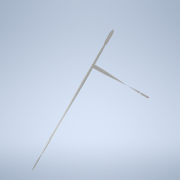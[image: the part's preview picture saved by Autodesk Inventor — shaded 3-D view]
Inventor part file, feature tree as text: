
AUTODESK INVENTOR PART (.ipt)
format: ipt  version: 2021 (Build 250183000, 183)  size: 4,764,160 bytes
history: native  units: in
note: dims shown in document units (in); Inventor stores cm internally (conversion verified against a paired STEP export)
features: imported_body x51, sketch x1
ambient origin geometry x8: Origin, YZ Plane, XZ Plane, XY Plane, X Axis, Y Axis, Z Axis, Center Point
bodies: Solid52 (feature_tree), Solid53 (feature_tree), Solid54 (feature_tree), Solid55 (feature_tree), Solid56 (feature_tree), Solid57 (feature_tree), Solid58 (feature_tree), Solid59 (feature_tree), Solid60 (feature_tree), Solid61 (feature_tree), Solid62 (feature_tree), Solid63 (feature_tree), Solid64 (feature_tree), Solid65 (feature_tree), Solid66 (feature_tree), Solid67 (feature_tree), Solid68 (feature_tree), Solid69 (feature_tree), Solid70 (feature_tree), Solid71 (feature_tree), Solid72 (feature_tree), Solid73 (feature_tree), Solid74 (feature_tree), Solid75 (feature_tree), Solid76 (feature_tree), Solid77 (feature_tree), Solid78 (feature_tree), Solid79 (feature_tree), Solid80 (feature_tree), Solid81 (feature_tree), Solid82 (feature_tree), Solid83 (feature_tree), Solid84 (feature_tree), Solid85 (feature_tree), Solid86 (feature_tree), Solid87 (feature_tree), Solid88 (feature_tree), Solid89 (feature_tree), Solid90 (feature_tree), Solid91 (feature_tree), Solid92 (feature_tree), Solid93 (feature_tree), Solid94 (feature_tree), Solid95 (feature_tree), Solid96 (feature_tree), Solid97 (feature_tree), Solid98 (feature_tree), Solid99 (feature_tree), Solid100 (feature_tree), Solid101 (feature_tree), Solid102 (feature_tree)
feature tree (52):
  imported_body  "Base52"
  sketch  "Sketch2"
  imported_body  "Base53"
  imported_body  "Base54"
  imported_body  "Base55"
  imported_body  "Base56"
  imported_body  "Base57"
  imported_body  "Base58"
  imported_body  "Base59"
  imported_body  "Base60"
  imported_body  "Base61"
  imported_body  "Base62"
  imported_body  "Base63"
  imported_body  "Base64"
  imported_body  "Base65"
  imported_body  "Base66"
  imported_body  "Base67"
  imported_body  "Base68"
  imported_body  "Base69"
  imported_body  "Base70"
  imported_body  "Base71"
  imported_body  "Base72"
  imported_body  "Base73"
  imported_body  "Base74"
  imported_body  "Base75"
  imported_body  "Base76"
  imported_body  "Base77"
  imported_body  "Base78"
  imported_body  "Base79"
  imported_body  "Base80"
  imported_body  "Base81"
  imported_body  "Base82"
  imported_body  "Base83"
  imported_body  "Base84"
  imported_body  "Base85"
  imported_body  "Base86"
  imported_body  "Base87"
  imported_body  "Base88"
  imported_body  "Base89"
  imported_body  "Base90"
  imported_body  "Base91"
  imported_body  "Base92"
  imported_body  "Base93"
  imported_body  "Base94"
  imported_body  "Base95"
  imported_body  "Base96"
  imported_body  "Base97"
  imported_body  "Base98"
  imported_body  "Base99"
  imported_body  "Base100"
  imported_body  "Base101"
  imported_body  "Base102"
